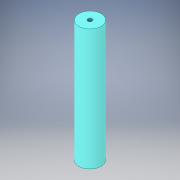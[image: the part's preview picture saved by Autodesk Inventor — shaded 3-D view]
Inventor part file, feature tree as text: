
AUTODESK INVENTOR PART (.ipt)
format: ipt  version: 2018 (Build 220112000, 112)  size: 115,200 bytes
history: native  units: in
note: dims shown in document units (in); Inventor stores cm internally (conversion verified against a paired STEP export)
features: sketch x3, hole x2, extrude x1
ambient origin geometry x8: Origin, YZ Plane, XZ Plane, XY Plane, X Axis, Y Axis, Z Axis, Center Point
bodies: Solid1 (feature_tree)
feature tree (6):
  extrude  "Extrusion1"  Depth=5.479in TaperAngle=0.0deg
  sketch  "Sketch3"  dims[d4=0.196in d5=0.5in d6=0.375in d7=0.25in d8=0.5635in d9=0.75in d10=0.8108in d11=0.5in d12=0.196in d13=0.5in d14=0.375in d15=0.25in d16=0.5635in d17=0.75in d18=0.8108in]
  hole  "Hole1"  [1 undecoded]
  hole  "Hole2"  [1 undecoded]
  sketch  "Sketch1"  dims[d0=1.0in d1=5.479in d2=0.0in]
  sketch  "Sketch2"  dims[d3=0.25in]
note: 2 required parameter values undecoded (feature->parameter linkage not recoverable at this tier; creation-order binding heuristic only, values carry confidence <= 0.55)
